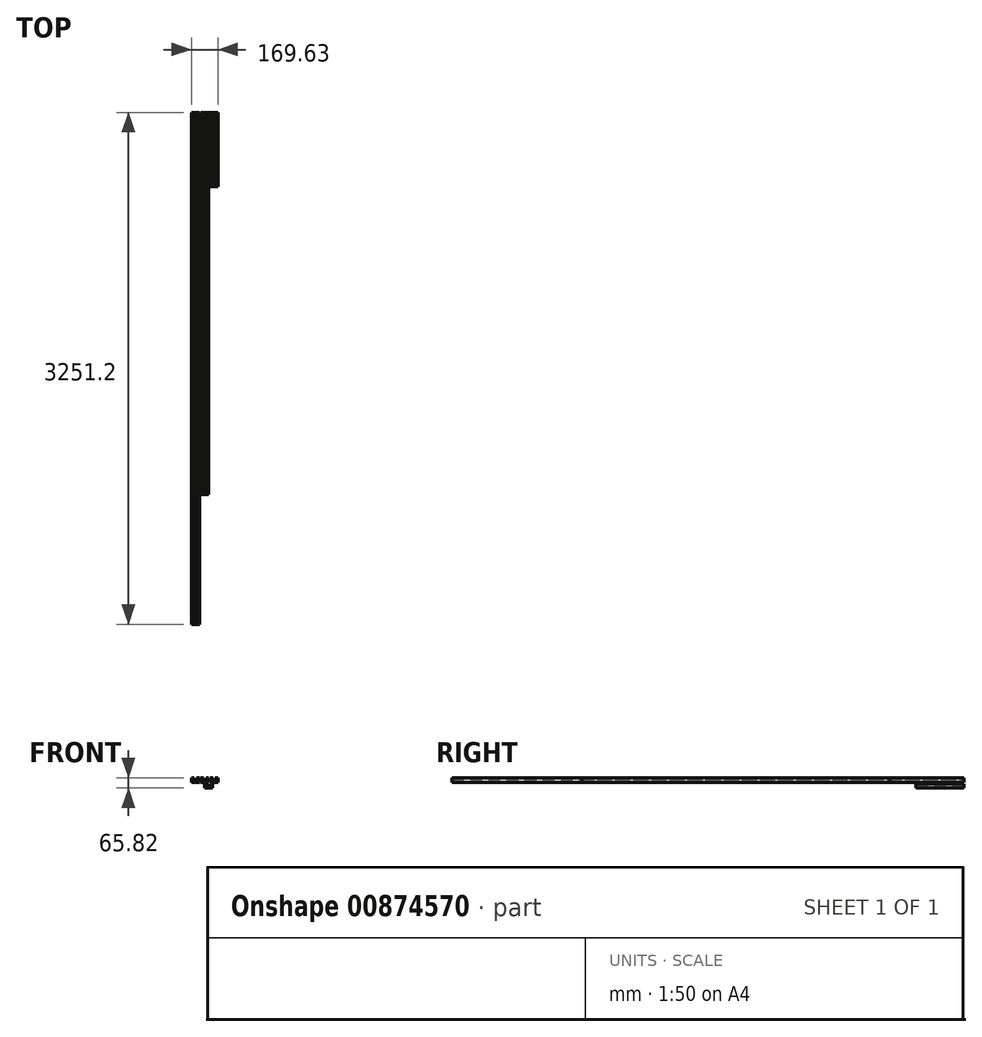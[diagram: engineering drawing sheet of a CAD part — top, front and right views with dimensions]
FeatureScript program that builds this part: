
annotation { "Feature Type Name" : "Feature", "Feature Type Description" : "" }
export const myFeature = defineFeature(function(context is Context, id is Id, definition is map)
    precondition{}
    {
        {
            var Q0;
            Q0=qCreatedBy(makeId("Front.planeOp"),FACE);
            var sketch = newSketch(context, id + "F0", { "sketchPlane" : qUnion([Q0])});
            skLineSegment(sketch, "E0", {"start": v(0, 0) * mm, "end": v(-25.4, 0) * mm});
            skLineSegment(sketch, "E1", {"start": v(-25.4, 0) * mm, "end": v(-25.4, 28.1) * mm});
            skLineSegment(sketch, "E2", {"start": v(-25.4, 28.1) * mm, "end": v(-7.92, 28.1) * mm});
            skLineSegment(sketch, "E3", {"start": v(-7.92, 28.1) * mm, "end": v(-7.92, 20.15) * mm});
            skLineSegment(sketch, "E4", {"start": v(-7.92, 20.15) * mm, "end": v(-12.7, 20.15) * mm});
            skLineSegment(sketch, "E5", {"start": v(-12.7, 20.15) * mm, "end": v(-12.7, 9.57) * mm});
            skLineSegment(sketch, "E6", {"start": v(-12.7, 9.57) * mm, "end": v(12.7, 9.57) * mm});
            skLineSegment(sketch, "E7", {"start": v(12.7, 9.57) * mm, "end": v(12.7, 20.15) * mm});
            skLineSegment(sketch, "E8", {"start": v(12.7, 20.15) * mm, "end": v(7.92, 20.15) * mm});
            skLineSegment(sketch, "E9", {"start": v(7.92, 20.15) * mm, "end": v(7.92, 28.1) * mm});
            skLineSegment(sketch, "E10", {"start": v(7.92, 28.1) * mm, "end": v(25.4, 28.1) * mm});
            skLineSegment(sketch, "E11", {"start": v(25.4, 28.1) * mm, "end": v(25.4, 0) * mm});
            skLineSegment(sketch, "E12", {"start": v(25.4, 0) * mm, "end": v(0, 0) * mm});
            skSolve(sketch);
        }
        {
            var Q0;
            Q0=qCreatedBy(makeId("Front.planeOp"),FACE);
            var sketch = newSketch(context, id + "F1", { "sketchPlane" : qUnion([Q0])});
            skLineSegment(sketch, "E13", {"start": v(-58.66, 0) * mm, "end": v(-84.06, 0) * mm});
            skLineSegment(sketch, "E14", {"start": v(-84.06, 0) * mm, "end": v(-84.06, 28.1) * mm});
            skLineSegment(sketch, "E15", {"start": v(-84.06, 28.1) * mm, "end": v(-66.58, 28.1) * mm});
            skLineSegment(sketch, "E16", {"start": v(-66.58, 28.1) * mm, "end": v(-66.58, 20.15) * mm});
            skLineSegment(sketch, "E17", {"start": v(-66.58, 20.15) * mm, "end": v(-71.36, 20.15) * mm});
            skLineSegment(sketch, "E18", {"start": v(-71.36, 20.15) * mm, "end": v(-71.36, 9.57) * mm});
            skLineSegment(sketch, "E19", {"start": v(-71.36, 9.57) * mm, "end": v(-45.96, 9.57) * mm});
            skLineSegment(sketch, "E20", {"start": v(-45.96, 9.57) * mm, "end": v(-45.96, 20.15) * mm});
            skLineSegment(sketch, "E21", {"start": v(-45.96, 20.15) * mm, "end": v(-50.73, 20.15) * mm});
            skLineSegment(sketch, "E22", {"start": v(-50.73, 20.15) * mm, "end": v(-50.73, 28.1) * mm});
            skLineSegment(sketch, "E23", {"start": v(-50.73, 28.1) * mm, "end": v(-33.26, 28.1) * mm});
            skLineSegment(sketch, "E24", {"start": v(-33.26, 28.1) * mm, "end": v(-33.26, 0) * mm});
            skLineSegment(sketch, "E25", {"start": v(-33.26, 0) * mm, "end": v(-58.66, 0) * mm});
            skSolve(sketch);
        }
        {
            var Q0;
            Q0=qCreatedBy(makeId("Front.planeOp"),FACE);
            var sketch = newSketch(context, id + "F2", { "sketchPlane" : qUnion([Q0])});
            skLineSegment(sketch, "E26", {"start": v(60.17, 0.24) * mm, "end": v(34.77, 0.24) * mm});
            skLineSegment(sketch, "E27", {"start": v(34.77, 0.24) * mm, "end": v(34.77, 28.34) * mm});
            skLineSegment(sketch, "E28", {"start": v(34.77, 28.34) * mm, "end": v(52.25, 28.34) * mm});
            skLineSegment(sketch, "E29", {"start": v(52.25, 28.34) * mm, "end": v(52.25, 20.4) * mm});
            skLineSegment(sketch, "E30", {"start": v(52.25, 20.4) * mm, "end": v(47.47, 20.4) * mm});
            skLineSegment(sketch, "E31", {"start": v(47.47, 20.4) * mm, "end": v(47.47, 9.81) * mm});
            skLineSegment(sketch, "E32", {"start": v(47.47, 9.81) * mm, "end": v(72.87, 9.81) * mm});
            skLineSegment(sketch, "E33", {"start": v(72.87, 9.81) * mm, "end": v(72.87, 20.4) * mm});
            skLineSegment(sketch, "E34", {"start": v(72.87, 20.4) * mm, "end": v(68.1, 20.4) * mm});
            skLineSegment(sketch, "E35", {"start": v(68.1, 20.4) * mm, "end": v(68.1, 28.34) * mm});
            skLineSegment(sketch, "E36", {"start": v(68.1, 28.34) * mm, "end": v(85.57, 28.34) * mm});
            skLineSegment(sketch, "E37", {"start": v(85.57, 28.34) * mm, "end": v(85.57, 0.24) * mm});
            skLineSegment(sketch, "E38", {"start": v(85.57, 0.24) * mm, "end": v(60.17, 0.24) * mm});
            skSolve(sketch);
        }
        {
            var Q0;
            Q0=qCreatedBy(makeId("Front.planeOp"),FACE);
            var sketch = newSketch(context, id + "F3", { "sketchPlane" : qUnion([Q0])});
            skLineSegment(sketch, "E39", {"start": v(25.4, -37.48) * mm, "end": v(0, -37.48) * mm});
            skLineSegment(sketch, "E40", {"start": v(0, -37.48) * mm, "end": v(0, -9.38) * mm});
            skLineSegment(sketch, "E41", {"start": v(0, -9.38) * mm, "end": v(17.48, -9.38) * mm});
            skLineSegment(sketch, "E42", {"start": v(17.48, -9.38) * mm, "end": v(17.48, -17.33) * mm});
            skLineSegment(sketch, "E43", {"start": v(17.48, -17.33) * mm, "end": v(12.7, -17.33) * mm});
            skLineSegment(sketch, "E44", {"start": v(12.7, -17.33) * mm, "end": v(12.7, -27.9) * mm});
            skLineSegment(sketch, "E45", {"start": v(12.7, -27.9) * mm, "end": v(38.1, -27.9) * mm});
            skLineSegment(sketch, "E46", {"start": v(38.1, -27.9) * mm, "end": v(38.1, -17.33) * mm});
            skLineSegment(sketch, "E47", {"start": v(38.1, -17.33) * mm, "end": v(33.32, -17.33) * mm});
            skLineSegment(sketch, "E48", {"start": v(33.32, -17.33) * mm, "end": v(33.32, -9.38) * mm});
            skLineSegment(sketch, "E49", {"start": v(33.32, -9.38) * mm, "end": v(50.8, -9.38) * mm});
            skLineSegment(sketch, "E50", {"start": v(50.8, -9.38) * mm, "end": v(50.8, -37.48) * mm});
            skLineSegment(sketch, "E51", {"start": v(50.8, -37.48) * mm, "end": v(25.4, -37.48) * mm});
            skSolve(sketch);
        }
        {
            var Q0;
            Q0=makeQuery(id+"F1.imprint","IMPRINT",FACE,{"disambiguationData":[TD([[makeQuery(id+"F1.imprint","IMPRINT",EDGE,{"derivedFrom":sQuery(id+"F1.wireOp",EDGE,"E13")}),-1.0]])]});
            extrude(context, id + "F4", {"entities" : qUnion([Q0]), "depth" : 3251.2 * mm, "offsetDistance" : 25.4 * mm});
        }
        {
            var Q0;
            Q0=makeQuery(id+"F0.imprint","IMPRINT",FACE,{"disambiguationData":[TD([[makeQuery(id+"F0.imprint","IMPRINT",EDGE,{"derivedFrom":sQuery(id+"F0.wireOp",EDGE,"E0")}),-1.0]])]});
            extrude(context, id + "F5", {"entities" : qUnion([Q0]), "depth" : 2425.7 * mm, "offsetDistance" : 25.4 * mm});
        }
        {
            var Q0;
            Q0=makeQuery(id+"F2.imprint","IMPRINT",FACE,{"disambiguationData":[TD([[makeQuery(id+"F2.imprint","IMPRINT",EDGE,{"derivedFrom":sQuery(id+"F2.wireOp",EDGE,"E26")}),-1.0]])]});
            extrude(context, id + "F6", {"entities" : qUnion([Q0]), "depth" : 469.9 * mm, "offsetDistance" : 25.4 * mm});
        }
        {
            var Q0;
            Q0=makeQuery(id+"F3.imprint","IMPRINT",FACE,{"disambiguationData":[TD([[makeQuery(id+"F3.imprint","IMPRINT",EDGE,{"derivedFrom":sQuery(id+"F3.wireOp",EDGE,"E39")}),-1.0]])]});
            extrude(context, id + "F7", {"entities" : qUnion([Q0]), "depth" : 304.8 * mm, "offsetDistance" : 25.4 * mm});
        }
    });
